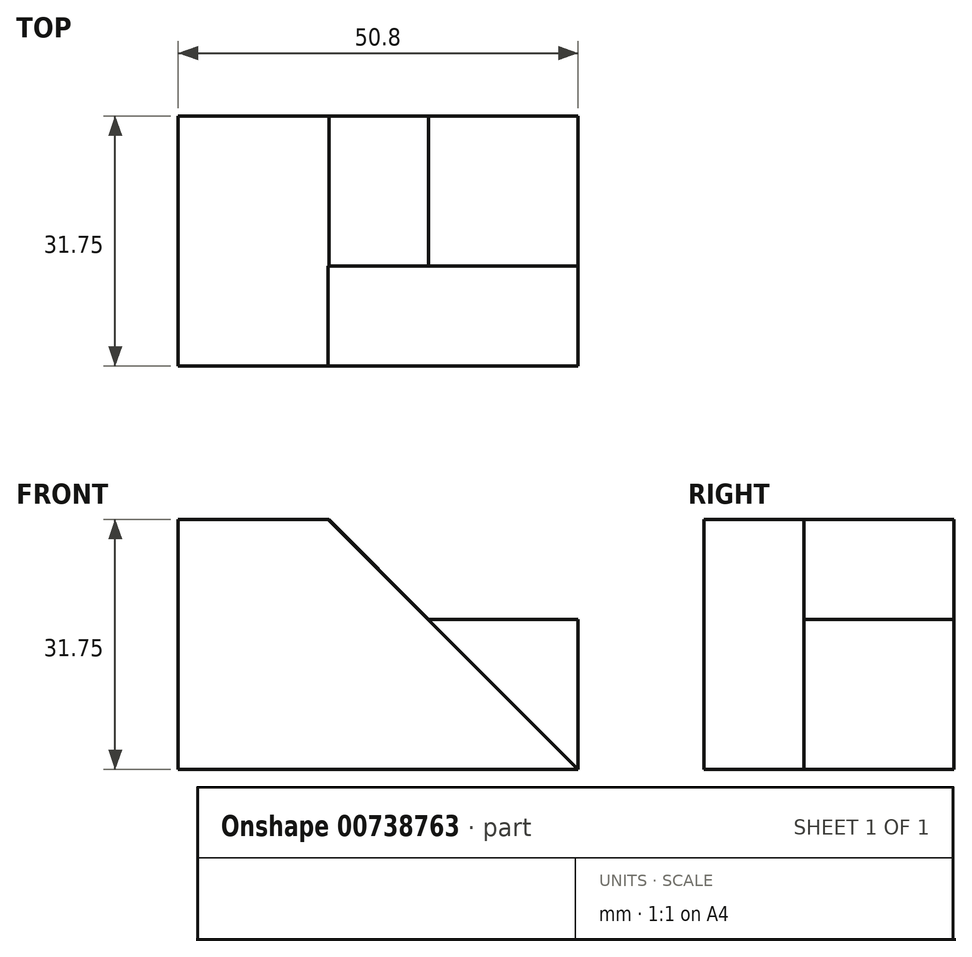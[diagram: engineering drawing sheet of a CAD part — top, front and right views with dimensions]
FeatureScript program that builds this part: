
annotation { "Feature Type Name" : "Feature", "Feature Type Description" : "" }
export const myFeature = defineFeature(function(context is Context, id is Id, definition is map)
    precondition{}
    {
        {
            var Q0;
            Q0=qCreatedBy(makeId("Front.planeOp"),FACE);
            var sketch = newSketch(context, id + "F0", { "sketchPlane" : qUnion([Q0])});
            skLineSegment(sketch, "E0", {"start": v(0, 0) * mm, "end": v(0, 31.75) * mm});
            skLineSegment(sketch, "E1", {"start": v(0, 31.75) * mm, "end": v(50.8, 31.75) * mm});
            skLineSegment(sketch, "E2", {"start": v(50.8, 31.75) * mm, "end": v(50.8, 0) * mm});
            skLineSegment(sketch, "E3", {"start": v(50.8, 0) * mm, "end": v(0, 0) * mm});
            skSolve(sketch);
        }
        {
            var Q0;
            Q0 = qSketchRegion(id + "F0", true);
            extrude(context, id + "F1", {"entities" : qUnion([Q0]), "oppositeDirection" : true, "depth" : 31.75 * mm, "offsetDistance" : 25.4 * mm});
        }
        {
            var Q0;
            Q0=qCreatedBy(makeId("Front.planeOp"),FACE);
            var sketch = newSketch(context, id + "F2", { "sketchPlane" : qUnion([Q0])});
            skLineSegment(sketch, "E4", {"start": v(19.05, 31.75) * mm, "end": v(50.8, 0) * mm});
            skLineSegment(sketch, "E5", {"start": v(50.8, 0) * mm, "end": v(50.8, 31.75) * mm});
            skLineSegment(sketch, "E6", {"start": v(50.8, 31.75) * mm, "end": v(19.05, 31.75) * mm});
            skSolve(sketch);
        }
        {
            var Q0;
            Q0 = qSketchRegion(id + "F2", true);
            extrude(context, id + "F3", {"entities" : qUnion([Q0]), "operationType" : NewBodyOperationType.REMOVE, "oppositeDirection" : true, "depth" : 12.7 * mm, "offsetDistance" : 25.4 * mm});
        }
        {
            var Q0;
            Q0=qCreatedBy(makeId("Front.planeOp"),FACE);
            var sketch = newSketch(context, id + "F4", { "sketchPlane" : qUnion([Q0])});
            skLineSegment(sketch, "E7", {"start": v(19.05, 31.88) * mm, "end": v(31.83, 19.05) * mm});
            skLineSegment(sketch, "E8", {"start": v(31.83, 19.05) * mm, "end": v(50.8, 19.05) * mm});
            skLineSegment(sketch, "E9", {"start": v(50.8, 19.05) * mm, "end": v(50.8, 31.75) * mm});
            skLineSegment(sketch, "E10", {"start": v(50.8, 31.75) * mm, "end": v(19.05, 31.88) * mm});
            skSolve(sketch);
        }
        {
            var Q0;
            Q0 = qSketchRegion(id + "F4", true);
            extrude(context, id + "F5", {"entities" : qUnion([Q0]), "operationType" : NewBodyOperationType.REMOVE, "endBound" : BoundingType.THROUGH_ALL, "oppositeDirection" : true, "depth" : 25.4 * mm, "offsetDistance" : 25.4 * mm});
        }
    });
